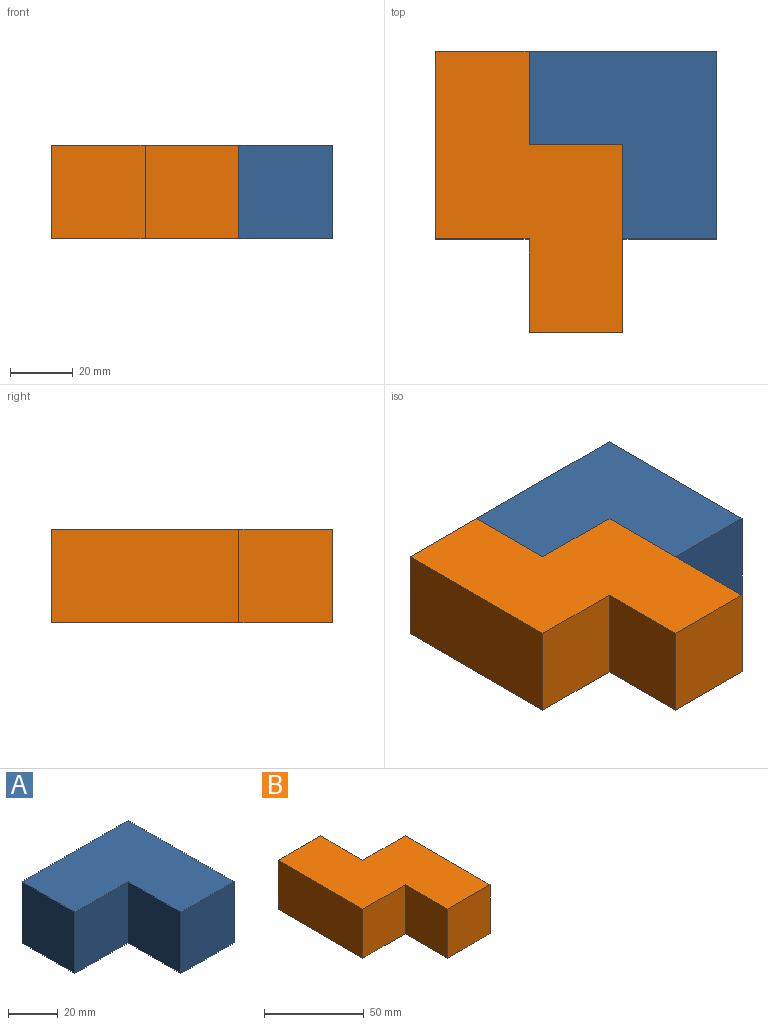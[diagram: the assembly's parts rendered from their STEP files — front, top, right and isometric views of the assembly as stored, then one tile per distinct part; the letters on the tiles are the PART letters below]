
ASSEMBLY  parts=2 mates=1
PART A: 8 faces, bbox 60x60x30 mm
  f0: plane 60x60mm, normal (0,0,1), area 2700mm2, adj f2,f3,f4,f5,f6,f7
  f1: plane 60x60mm, normal (0,0,-1), area 2700mm2, adj f2,f3,f4,f5,f6,f7
  f2: plane 60x30mm, normal (1,0,0), area 1800mm2, adj f0,f1,f5,f7
  f3: plane 30x30mm, normal (-1,0,0), area 900mm2, adj f0,f1,f4,f7
  f4: plane 30x30mm, normal (0,-1,0), area 900mm2, adj f0,f1,f3,f6
  f5: plane 60x30mm, normal (0,1,0), area 1800mm2, adj f0,f1,f2,f6
  f6: plane 30x30mm, normal (-1,0,0), area 900mm2, adj f0,f1,f4,f5
  f7: plane 30x30mm, normal (0,-1,0), area 900mm2, adj f0,f1,f2,f3
PART B: 10 faces, bbox 60x90x30 mm
  f0: plane 30x30mm, normal (1,0,0), area 900mm2, adj f1,f3,f4,f6
  f1: plane 30x30mm, normal (0,1,0), area 900mm2, adj f0,f2,f3,f4
  f2: plane 60x30mm, normal (-1,0,0), area 1800mm2, adj f1,f3,f4,f5
  f3: plane 90x60mm, normal (0,0,1), area 3600mm2, adj f0,f1,f2,f5,f6,f7,f8,f9
  f4: plane 90x60mm, normal (0,0,-1), area 3600mm2, adj f0,f1,f2,f5,f6,f7,f8,f9
  f5: plane 30x30mm, normal (0,-1,0), area 900mm2, adj f2,f3,f4,f8
  f6: plane 30x30mm, normal (0,1,0), area 900mm2, adj f0,f3,f4,f7
  f7: plane 60x30mm, normal (1,0,0), area 1800mm2, adj f3,f4,f6,f9
  f8: plane 30x30mm, normal (-1,0,0), area 900mm2, adj f3,f4,f5,f9
  f9: plane 30x30mm, normal (0,-1,0), area 900mm2, adj f3,f4,f7,f8
PLACE A t=(20,2.78,-15.16)mm
PLACE B t=(20,2.78,-15.16)mm
MATE fastened A.f6 <-> B.f0  axis (-1,0,0) through (5,32.78,-0.16)mm
